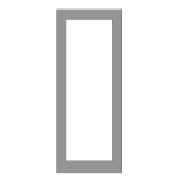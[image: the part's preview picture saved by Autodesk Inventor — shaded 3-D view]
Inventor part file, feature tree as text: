
AUTODESK INVENTOR PART (.ipt)
format: ipt  version: 2020 (Build 240168000, 168)  size: 131,072 bytes
history: native  units: in
note: dims shown in document units (in); Inventor stores cm internally (conversion verified against a paired STEP export)
features: other x4, plane x3, sketch x3, split x2
ambient origin geometry x8: Origin, YZ Plane, XZ Plane, XY Plane, X Axis, Y Axis, Z Axis, Center Point
bodies: Solid1 (feature_tree), Body (feature_tree)
feature tree (12):
  other  "Driven Length"
  other  "Frame Generator"
  other  "Start Plane"
  other  "End Plane"
  plane  "Work Plane6"
  split  "Split1"
  plane  "Work Plane7"
  split  "Split2"
  sketch  "Sketch"  dims[d2=0.125in d3=0.125in d6=0.5in d7=24.5in d8=0.13in d9=0.0in d14=90.0deg d11=24.0in]
  sketch  "Sketch6"  dims[d0=1.0in]
  plane  "Work Plane5"
  sketch  "Sketch7"  dims[d1=3.0in]
